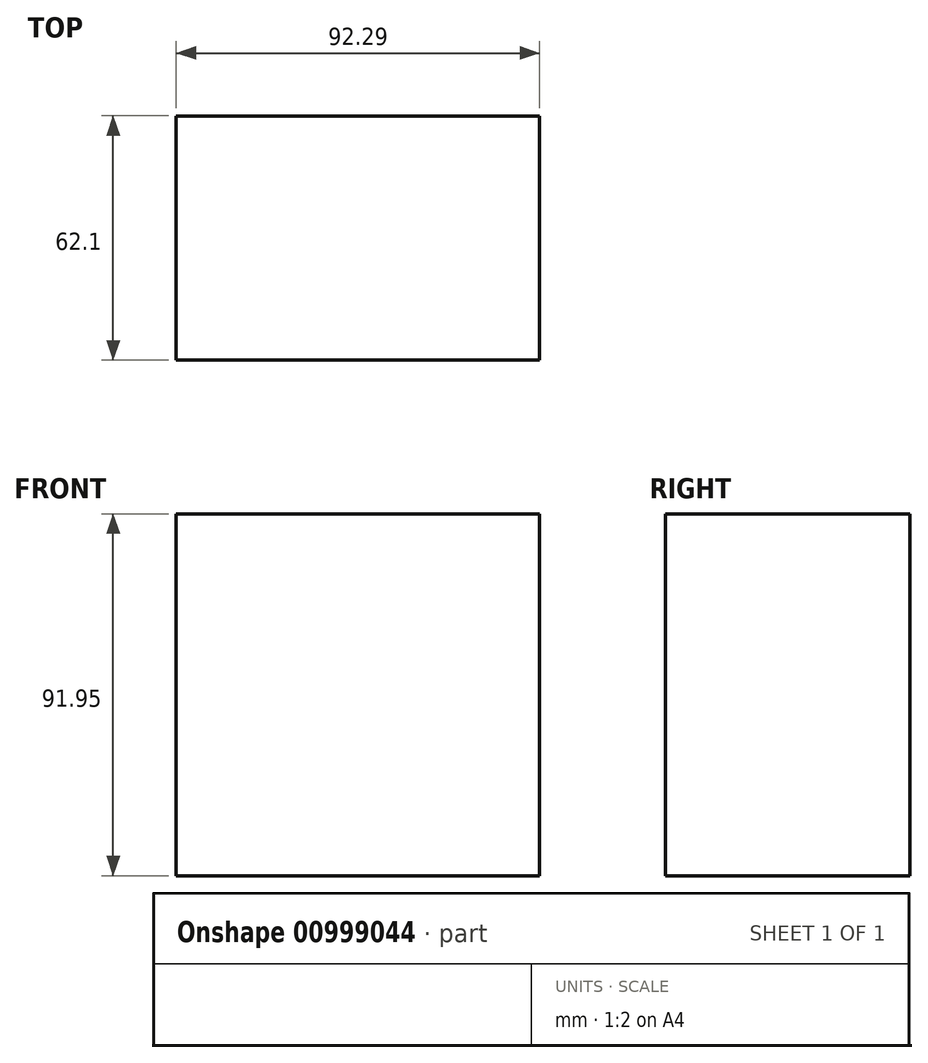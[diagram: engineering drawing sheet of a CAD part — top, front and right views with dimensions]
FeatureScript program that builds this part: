
annotation { "Feature Type Name" : "Feature", "Feature Type Description" : "" }
export const myFeature = defineFeature(function(context is Context, id is Id, definition is map)
    precondition{}
    {
        {
            var Q0;
            Q0=qCreatedBy(makeId("Top.planeOp"),FACE);
            var sketch = newSketch(context, id + "F0", { "sketchPlane" : qUnion([Q0])});
            skLineSegment(sketch, "E0.bottom", {"start": v(-57.73, -40.16) * mm, "end": v(34.56, -40.16) * mm});
            skLineSegment(sketch, "E0.top", {"start": v(-57.73, 21.94) * mm, "end": v(34.56, 21.94) * mm});
            skLineSegment(sketch, "E0.left", {"start": v(-57.73, -40.16) * mm, "end": v(-57.73, 21.94) * mm});
            skLineSegment(sketch, "E0.right", {"start": v(34.56, -40.16) * mm, "end": v(34.56, 21.94) * mm});
            skSolve(sketch);
        }
        {
            var Q0;
            Q0=makeQuery(id+"F0.imprint","IMPRINT",FACE,{"disambiguationData":[TD([[makeQuery(id+"F0.imprint","IMPRINT",EDGE,{"derivedFrom":sQuery(id+"F0.wireOp",EDGE,"E0.bottom")}),1.0]])]});
            extrude(context, id + "F1", {"entities" : qUnion([Q0]), "depth" : 91.95 * mm, "offsetDistance" : 25.4 * mm});
        }
    });
